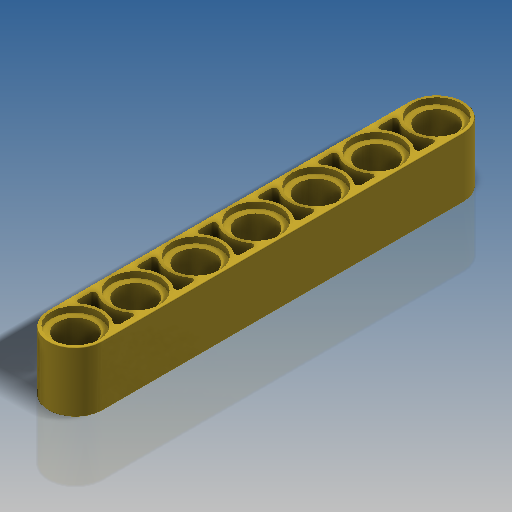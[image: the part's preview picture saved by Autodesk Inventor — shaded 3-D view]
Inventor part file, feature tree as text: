
AUTODESK INVENTOR PART (.ipt)
format: ipt  version: 2018.3 (Build 223284000, 284)  size: 410,624 bytes
history: native  units: mm
features: extrude x3, sketch x2, mirror x1, fillet x1
ambient origin geometry x8: Origin, YZ Plane, XZ Plane, XY Plane, X Axis, Y Axis, Z Axis, Center Point
bodies: Solid1 (feature_tree)
feature tree (7):
  extrude  "Extrusion1"  Depth=7.2mm
  sketch  "Sketch6"  dims[d41=0.8mm d42=0.0mm d43=3.1mm d44=0.0mm d48=48.0mm d49=6.4mm d50=4.8mm d51=8.0mm d52=0.8mm d53=60.0mm d55=8.0mm d56=10.0mm d58=10.0mm d60=0.4mm d61=0.1mm]
  extrude  "Extrusion7"  Depth=3.1mm TaperAngle=0.0deg
  extrude  "Extrusion8"  Depth=0.1mm
  mirror  "Mirror1"
  fillet  "Fillet2"  Radius=6.4mm
  sketch  "Sketch1"  dims[d14=8.0mm d15=0.0mm d32=7.2mm]
